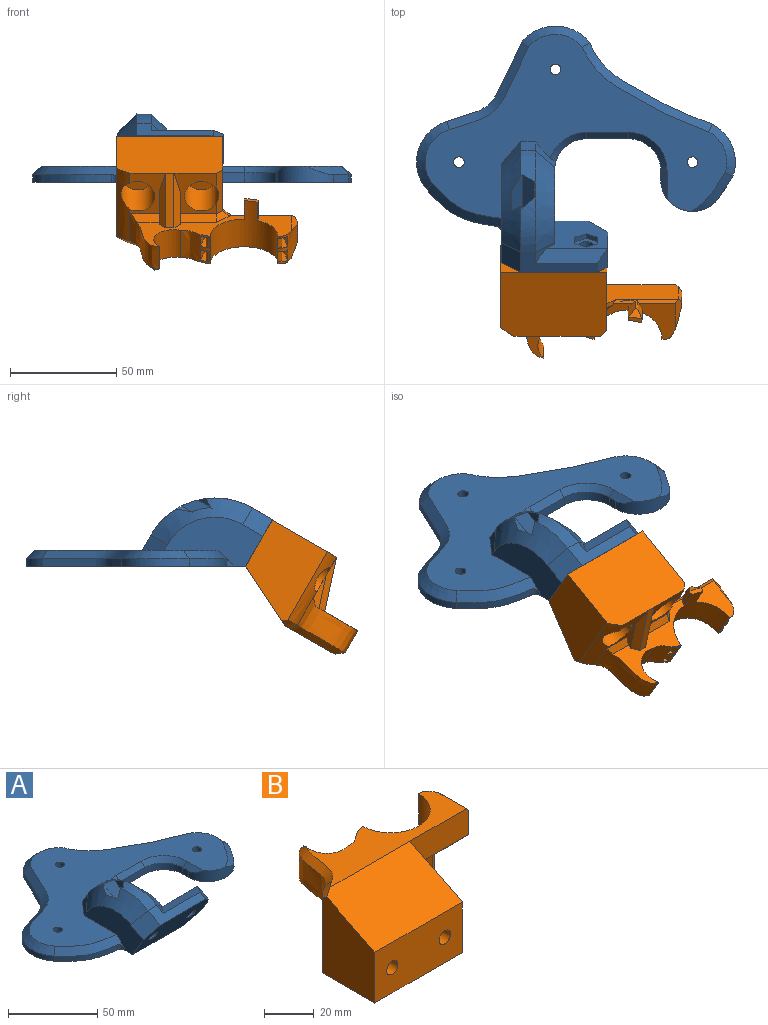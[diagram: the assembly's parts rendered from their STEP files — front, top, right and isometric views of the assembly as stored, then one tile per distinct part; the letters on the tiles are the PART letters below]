
ASSEMBLY  parts=2 mates=1
PART A: 68 faces, bbox 151.9x117.9x33.9 mm
  f0: cylinder r=5mm len=10mm, axis (0,0,-1), area 94.2mm2, adj f16,f26
  f1: cylinder r=5mm len=10mm, axis (0,0,-1), area 94.2mm2, adj f16,f24
  f2: cylinder r=5mm len=10mm, axis (0,0,-1), area 94.2mm2, adj f16,f22
  f3: cylinder r=15mm len=15mm, axis (0,0,-1), area 106mm2, adj f4,f14,f16,f54
  f4: plane 4.5x4.21mm, normal (-1,0,0), area 18.9mm2, adj f3,f16,f55,f56
  f5: extruded ~10.77x7.22mm, area 45.4mm2, adj f6,f16,f27,f56
  f6: cylinder r=20.18mm len=24.6mm, axis (0,0,-1), area 101mm2, adj f5,f7,f16,f28
  f7: extruded ~57.67x38.27mm, area 248.5mm2, adj f6,f8,f16,f29
  f8: cylinder r=20.47mm len=32.11mm, axis (0,0,-1), area 129.2mm2, adj f7,f9,f16,f30
  f9: extruded ~37.43x35.24mm, area 192mm2, adj f8,f10,f16,f32
  f10: cylinder r=20mm len=31.78mm, axis (0,0,-1), area 137.4mm2, adj f9,f11,f16,f33
  f11: extruded ~32.88x17.54mm, area 134.6mm2, adj f10,f16,f31,f67
  f12: plane 39.75x23.63mm, normal (1,0,0), area 634.4mm2, adj f13,f16,f34,f52,f61,f62,f63
  f13: cylinder r=15mm len=15mm, axis (0,0,-1), area 106mm2, adj f12,f14,f16,f52
  f14: plane 20x4.5mm, normal (0,-1,0), area 90mm2, adj f3,f13,f16,f53
  f15: plane 143.93x88.37mm, normal (0,0,1), area 4828.2mm2, adj f18,f19,f21,f23,f25,f27,f28,f29
  f16: plane 150.18x103.43mm, normal (0,0,-1), area 7297.1mm2, adj f0,f1,f2,f3,f4,f5,f6,f7
  f17: plane 50x21.97mm, normal (0,-0.87,-0.5), area 1102.4mm2, adj f16,f18,f20,f35,f36,f37,f60,f64
  f18: plane 46.58x23.16mm, normal (-1,0,0), area 619.7mm2, adj f15,f16,f17,f31,f58,f59,f60,f67
  f19: plane 7.16x7mm, normal (0,0.87,0.5), area 57.9mm2, adj f15,f57,f58,f61
  f20: plane 36x9.53mm, normal (0,-0.5,0.87), area 222mm2, adj f17,f57,f60,f63,f65,f66
  f21: cylinder r=2.5mm len=5mm, axis (0,0,-1), area 70.7mm2, adj f15,f22
  f22: plane 10x10mm, normal (0,0,-1), area 58.9mm2, adj f2,f21
  f23: cylinder r=2.5mm len=5mm, axis (0,0,-1), area 70.7mm2, adj f15,f24
  f24: plane 10x10mm, normal (0,0,-1), area 58.9mm2, adj f1,f23
  f25: cylinder r=2.5mm len=5mm, axis (0,0,-1), area 70.7mm2, adj f15,f26
  f26: plane 10x10mm, normal (0,0,-1), area 58.9mm2, adj f0,f25
  f27: bspline ~25.08x23.07mm, area 107.9mm2, adj f5,f15,f28,f56
  f28: cone r=20.18mm half-angle=45deg, axis (0,0,-1), area 145mm2, adj f6,f15,f27,f29
  f29: bspline ~65.16x43.96mm, area 408.8mm2, adj f7,f15,f28,f30
  f30: cone r=20.47mm half-angle=45deg, axis (0,0,-1), area 185.7mm2, adj f8,f15,f29,f32
  f31: bspline ~38.19x23.22mm, area 227.7mm2, adj f11,f15,f18,f33,f67
  f32: bspline ~43.84x40.12mm, area 318.2mm2, adj f9,f15,f30,f33
  f33: cone r=20mm half-angle=45deg, axis (0,0,-1), area 199.5mm2, adj f10,f15,f31,f32
  f34: plane 29x22.64mm, normal (0,0.87,0.5), area 513.3mm2, adj f12,f16,f35,f45,f46,f47,f48,f49
  f35: plane 16.54x13.64mm, normal (1,0,0), area 128.6mm2, adj f17,f34,f64,f65
  f36: cylinder r=3.25mm len=9.75mm, axis (0,-0.87,-0.5), area 153.2mm2, adj f17,f51
  f37: cylinder r=3.25mm len=9.75mm, axis (0,-0.87,-0.5), area 153.2mm2, adj f17,f44
  f38: plane 31.51x19.18mm, normal (-1,0,0), area 189.8mm2, adj f39,f43,f44,f57
  f39: plane 25.64x14.8mm, normal (-0.5,0.43,-0.75), area 160.8mm2, adj f38,f40,f44,f57
  f40: plane 21.67x14.72mm, normal (0.5,0.43,-0.75), area 142.6mm2, adj f39,f41,f44,f57,f59
  f41: plane 26.78x15.65mm, normal (1,0,0), area 151.6mm2, adj f40,f42,f44,f59
  f42: plane 31.97x18.09mm, normal (0.5,-0.43,0.75), area 197.3mm2, adj f41,f43,f44,f57,f59
  f43: plane 31.6x19.17mm, normal (-0.5,-0.43,0.75), area 210.7mm2, adj f38,f42,f44,f57
  f44: plane 10.83x10.83mm, normal (0,0.87,0.5), area 68.3mm2, adj f37,f38,f39,f40,f41,f42,f43
  f45: plane 6.66x5.29mm, normal (-1,0,0), area 15.6mm2, adj f34,f46,f50,f51
  f46: plane 5.41x3.96mm, normal (-0.5,0.43,-0.75), area 15.6mm2, adj f34,f45,f47,f51
  f47: plane 5.41x3.96mm, normal (0.5,0.43,-0.75), area 15.6mm2, adj f34,f46,f48,f51
  f48: plane 6.66x5.29mm, normal (1,0,0), area 15.6mm2, adj f34,f47,f49,f51
  f49: plane 5.41x3.96mm, normal (0.5,-0.43,0.75), area 15.6mm2, adj f34,f48,f50,f51
  f50: plane 5.41x3.96mm, normal (-0.5,-0.43,0.75), area 15.6mm2, adj f34,f45,f49,f51
  f51: plane 10.83x10.83mm, normal (0,0.87,0.5), area 68.3mm2, adj f36,f45,f46,f47,f48,f49,f50
  f52: cone r=15mm half-angle=45deg, axis (0,0,1), area 91mm2, adj f12,f13,f15,f53,f61
  f53: plane 20x3mm, normal (0,-0.71,0.71), area 84.9mm2, adj f14,f15,f52,f54
  f54: cone r=15mm half-angle=45deg, axis (0,0,1), area 110mm2, adj f3,f15,f53,f55
  f55: plane 14.67x4.46mm, normal (-0.71,0,0.71), area 43.9mm2, adj f4,f15,f54,f56
  f56: cylinder r=15mm len=26.83mm, axis (0,0,-1), area 235.6mm2, adj f4,f5,f15,f16,f27,f55
  f57: cylinder r=35mm len=47.81mm, axis (1,0,0), area 301.6mm2, adj f19,f20,f38,f39,f40,f42,f43,f59
  f58: plane 11.93x9mm, normal (-0.71,0.61,0.35), area 72.2mm2, adj f15,f18,f19,f59
  f59: cone r=26mm half-angle=45deg, axis (1,0,0), area 534.3mm2, adj f18,f40,f41,f42,f57,f58,f60
  f60: plane 14.03x13.29mm, normal (-0.71,-0.35,0.61), area 140mm2, adj f17,f18,f20,f59
  f61: plane 11.96x9.53mm, normal (0.71,0.61,0.35), area 76.2mm2, adj f12,f15,f19,f52,f62
  f62: cone r=26mm half-angle=45deg, axis (-1,0,0), area 609.8mm2, adj f12,f57,f61,f63
  f63: plane 9.7x9mm, normal (0.71,-0.35,0.61), area 30.4mm2, adj f12,f20,f34,f62,f66
  f64: plane 16.74x9mm, normal (0.71,0,-0.71), area 147mm2, adj f16,f17,f34,f35
  f65: plane 11.16x6.83mm, normal (0.71,-0.35,0.61), area 53mm2, adj f17,f20,f35,f66
  f66: plane 34x6.83mm, normal (0,0.26,0.97), area 205.1mm2, adj f20,f34,f63,f65
  f67: cylinder r=3mm len=3.5mm, axis (0,0,-1), area 11.1mm2, adj f11,f16,f18,f31
PART B: 59 faces, bbox 88.5x63.1x42 mm
  f0: plane 19.63x17.14mm, normal (0,0,-1), area 200.4mm2, adj f6,f7,f13,f41,f43,f48
  f1: plane 52.7x29.57mm, normal (0,0,-1), area 393.1mm2, adj f2,f7,f8,f9,f11,f16,f17,f33
  f2: extruded ~26.07x15mm, area 387.1mm2, adj f1,f3,f9,f34,f45
  f3: extruded ~37x6.27mm, area 245.5mm2, adj f2,f18,f20,f35,f50,f55
  f4: plane 33.72x18mm, normal (0,-1,0), area 464.2mm2, adj f10,f19,f39,f40,f48,f49
  f5: plane 9x3.5mm, normal (1,0,0), area 31.5mm2, adj f6,f40,f41,f49
  f6: extruded ~16.02x15mm, area 212.1mm2, adj f0,f5,f7,f10,f21,f23,f24,f25
  f7: cylinder r=16mm len=32mm, axis (0,0,-1), area 816.7mm2, adj f0,f1,f6,f8,f10,f11,f13,f14
  f8: extruded ~15x13.96mm, area 183mm2, adj f1,f7,f9,f10,f21,f23,f24,f25
  f9: cylinder r=9.5mm len=16.22mm, axis (0,0,-1), area 374.7mm2, adj f1,f2,f8,f10,f34
  f10: plane 78.67x27.45mm, normal (0,0,1), area 960.1mm2, adj f4,f6,f7,f8,f9,f34,f35,f40
  f11: plane 10x1.75mm, normal (-1,0,0), area 17.5mm2, adj f1,f7,f14,f42
  f12: cylinder r=21mm len=8.21mm, axis (0,0,1), area 9.8mm2, adj f42,f43,f44,f48
  f13: plane 10x1.62mm, normal (0.92,0.38,0), area 17.5mm2, adj f0,f7,f14,f43
  f14: plane 6.79x3.22mm, normal (0,0,-1), area 13.3mm2, adj f7,f11,f13,f42,f43,f44
  f15: plane 22x20mm, normal (0,1,0), area 192.9mm2, adj f16,f20,f36,f37,f46,f57
  f16: plane 15.16x4.85mm, normal (1,0,0), area 32.3mm2, adj f1,f15,f36,f46
  f17: plane 15.16x4.85mm, normal (-1,0,0), area 32.3mm2, adj f1,f18,f45,f47
  f18: plane 22x16.73mm, normal (0,1,0), area 158.9mm2, adj f3,f17,f20,f45,f47,f55
  f19: plane 40x32mm, normal (1,0,0), area 1019mm2, adj f4,f20,f37,f39,f51,f52
  f20: plane 50x35mm, normal (0,0,-1), area 1731.4mm2, adj f3,f15,f18,f19,f33,f37,f50,f51
  f21: plane 40.93x20.54mm, normal (0,0,-1), area 148.4mm2, adj f6,f7,f8,f22,f24,f30,f32
  f22: cylinder r=18mm len=35.71mm, axis (0,0,1), area 285.9mm2, adj f21,f23,f30,f32
  f23: plane 40.93x20.54mm, normal (0,0,1), area 148.4mm2, adj f6,f7,f8,f22,f24,f30,f32
  f24: cylinder r=20.5mm len=40.86mm, axis (0,0,1), area 335.9mm2, adj f6,f8,f21,f23
  f25: plane 40.93x20.54mm, normal (0,0,-1), area 148.4mm2, adj f6,f7,f8,f26,f28,f29,f31
  f26: cylinder r=18mm len=35.71mm, axis (0,0,1), area 285.9mm2, adj f25,f27,f29,f31
  f27: plane 40.93x20.54mm, normal (0,0,1), area 148.4mm2, adj f6,f7,f8,f26,f28,f29,f31
  f28: cylinder r=20.5mm len=40.86mm, axis (0,0,1), area 335.9mm2, adj f6,f8,f25,f27
  f29: cylinder r=2mm len=5.5mm, axis (0,0,-1), area 18mm2, adj f7,f25,f26,f27
  f30: cylinder r=2mm len=5.5mm, axis (0,0,-1), area 18mm2, adj f7,f21,f22,f23
  f31: cylinder r=2mm len=5.5mm, axis (0,0,-1), area 15.6mm2, adj f8,f25,f26,f27
  f32: cylinder r=2mm len=5.5mm, axis (0,0,-1), area 15.6mm2, adj f8,f21,f22,f23
  f33: plane 25x8mm, normal (0,0.95,-0.3), area 105mm2, adj f1,f20,f46,f47
  f34: bspline ~28.61x15.08mm, area 125mm2, adj f2,f9,f10,f35
  f35: bspline ~9.22x8.44mm, area 33.9mm2, adj f3,f10,f34,f50,f52
  f36: plane 17x3mm, normal (0,0.71,-0.71), area 72.1mm2, adj f1,f15,f16,f38
  f37: plane 24x5mm, normal (0.71,0.71,0), area 85.9mm2, adj f15,f19,f20,f38,f57
  f38: plane 6x6mm, normal (0.58,0.58,-0.58), area 23.4mm2, adj f1,f36,f37,f39
  f39: plane 4.5x4.5mm, normal (0.71,0,-0.71), area 10.1mm2, adj f1,f4,f19,f38,f48
  f40: plane 16.2x3.62mm, normal (0.71,0,0.71), area 43.5mm2, adj f4,f5,f6,f10,f49
  f41: plane 16.2x3.63mm, normal (0.71,0,-0.71), area 41.9mm2, adj f0,f5,f6,f48,f49
  f42: plane 11.49x3.78mm, normal (-0.65,-0.76,0), area 40.8mm2, adj f1,f11,f12,f14,f44,f48
  f43: plane 11.25x4.35mm, normal (0.89,-0.46,0), area 40.2mm2, adj f0,f12,f13,f14,f44,f48
  f44: cone r=21mm half-angle=45deg, axis (0,0,1), area 17mm2, adj f12,f14,f42,f43
  f45: plane 14.02x3.29mm, normal (0,0.71,-0.71), area 50.4mm2, adj f1,f2,f17,f18
  f46: plane 25x8mm, normal (0.71,0.67,-0.22), area 89.4mm2, adj f1,f15,f16,f33
  f47: plane 25x8mm, normal (-0.71,0.67,-0.22), area 89.4mm2, adj f1,f17,f18,f33
  f48: plane 30.74x1.52mm, normal (0,-0.71,-0.71), area 58.6mm2, adj f0,f1,f4,f12,f39,f41,f42,f43
  f49: plane 12x1.5mm, normal (0.71,-0.71,0), area 22.3mm2, adj f4,f5,f40,f41
  f50: plane 38.75x30mm, normal (-1,0,0), area 971.3mm2, adj f3,f20,f35,f51,f52
  f51: plane 50x25mm, normal (0,-1,0), area 1183.6mm2, adj f19,f20,f50,f52,f53,f54
  f52: plane 50.04x30.04mm, normal (0,-0.45,0.89), area 1671.1mm2, adj f10,f19,f35,f50,f51
  f53: cylinder r=3.25mm len=15mm, axis (0,-1,0), area 306.3mm2, adj f51,f58
  f54: cylinder r=3.25mm len=15mm, axis (0,-1,0), area 306.3mm2, adj f51,f56
  f55: cylinder r=8mm len=20mm, axis (0,-1,0), area 972.2mm2, adj f3,f18,f56
  f56: plane 16x16mm, normal (0,1,0), area 167.9mm2, adj f54,f55
  f57: cylinder r=8mm len=20mm, axis (0,-1,0), area 1005.3mm2, adj f15,f37,f58
  f58: plane 16x16mm, normal (0,1,0), area 167.9mm2, adj f53,f57
PLACE A t=(25.43,16.12,8.08)mm
PLACE B rot(axis=(-1,0,0),150deg) t=(105.04,-67.36,-17.34)mm
MATE planar A.f17 <-> B.f51  axis (0,-0.87,-0.5) through (70.04,-29.44,18.99)mm
